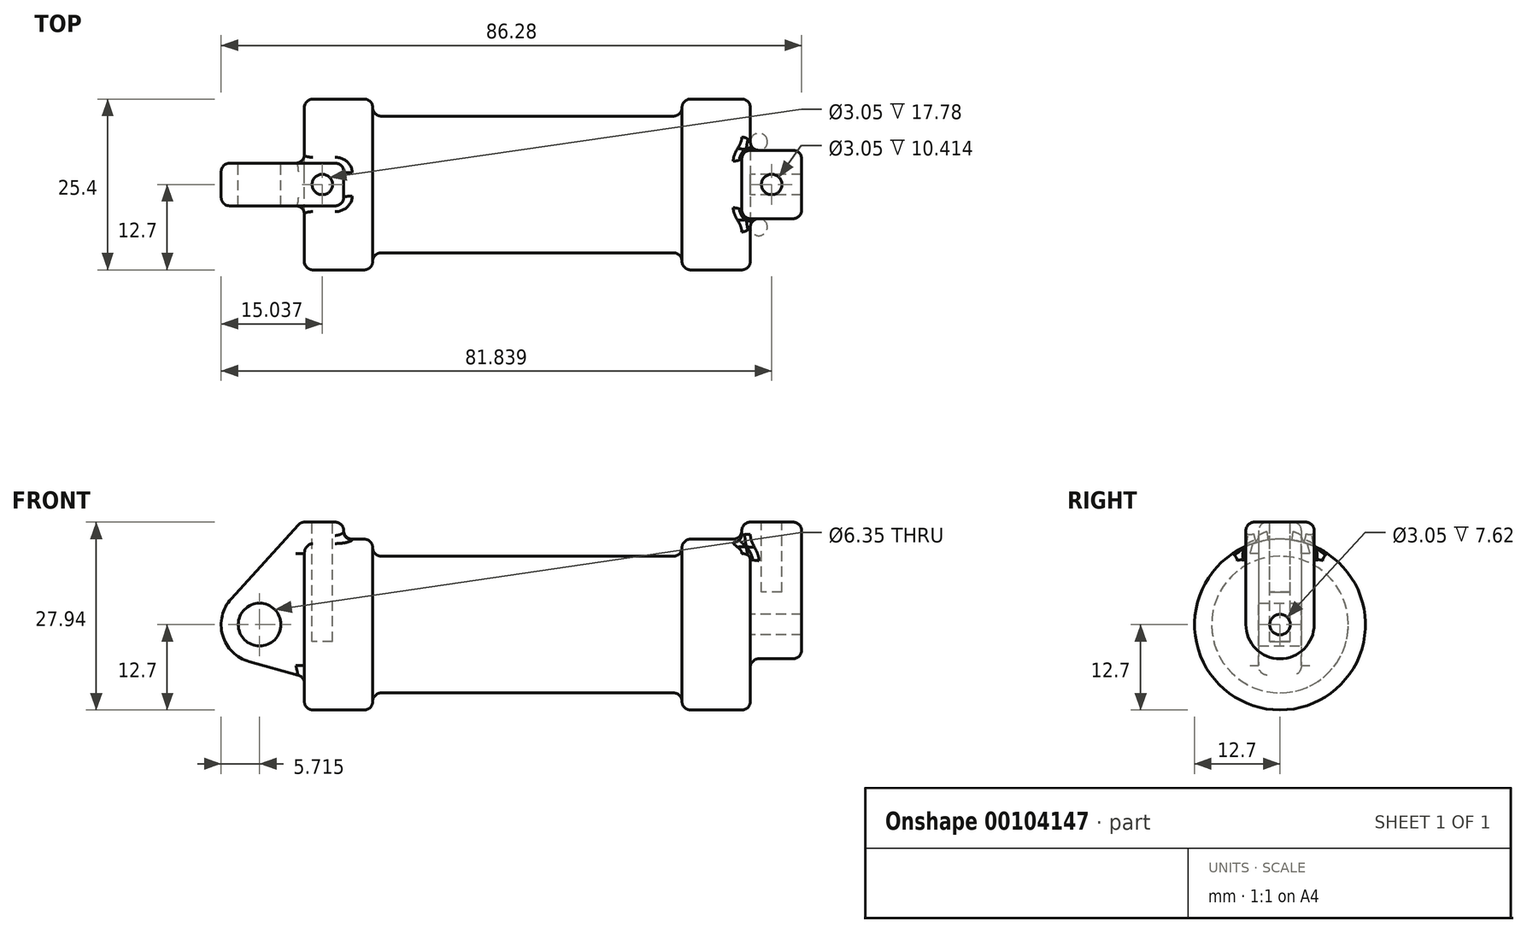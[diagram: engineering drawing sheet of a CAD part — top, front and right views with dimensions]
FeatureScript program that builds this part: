
annotation { "Feature Type Name" : "Feature", "Feature Type Description" : "" }
export const myFeature = defineFeature(function(context is Context, id is Id, definition is map)
    precondition{}
    {
        {
            var Q0;
            Q0=qCreatedBy(makeId("Front.planeOp"),FACE);
            var sketch = newSketch(context, id + "F0", { "sketchPlane" : qUnion([Q0])});
            skLineSegment(sketch, "E0", {"start": v(0, 0) * mm, "end": v(0, 12.7) * mm});
            skLineSegment(sketch, "E1", {"start": v(0, 12.7) * mm, "end": v(10.16, 12.7) * mm});
            skLineSegment(sketch, "E2", {"start": v(10.16, 12.7) * mm, "end": v(10.16, 10.16) * mm});
            skLineSegment(sketch, "E3", {"start": v(10.16, 10.16) * mm, "end": v(56.13, 10.16) * mm});
            skLineSegment(sketch, "E4", {"start": v(56.13, 10.16) * mm, "end": v(56.13, 12.7) * mm});
            skLineSegment(sketch, "E5", {"start": v(56.13, 12.7) * mm, "end": v(66.3, 12.7) * mm});
            skLineSegment(sketch, "E6", {"start": v(66.3, 12.7) * mm, "end": v(66.3, 0) * mm});
            skLineSegment(sketch, "E7", {"start": v(66.3, 0) * mm, "end": v(0, 0) * mm});
            skLineSegment(sketch, "E8", {"start": v(5.84, 15.24) * mm, "end": v(-0.5, 15.24) * mm});
            skLineSegment(sketch, "E9", {"start": v(-0.5, 15.24) * mm, "end": v(-10.88, 3.85) * mm});
            skLineSegment(sketch, "E10", {"start": v(0, 0) * mm, "end": v(-6.65, 0) * mm});
            skCircle(sketch, "E11", {"center": v(-6.65, 0) * mm, "radius": 5.72 * mm});
            skCircle(sketch, "E12", {"center": v(-6.65, 0) * mm, "radius": 3.18 * mm});
            skLineSegment(sketch, "E13", {"start": v(5.84, 15.24) * mm, "end": v(5.84, -9.4) * mm});
            skLineSegment(sketch, "E14", {"start": v(5.84, -9.4) * mm, "end": v(-8.18, -5.5) * mm});
            skSolve(sketch);
        }
        {
            var Q0;
            {var subQ0=sQuery(id+"F0.wireOp",EDGE,"E0");Q0=makeQuery(id+"F0.imprint","IMPRINT",FACE,{"disambiguationData":[TD([[makeQuery(id+"F0.imprint","IMPRINT",EDGE,{"derivedFrom":subQ0}),-1.0]])]});}
            var Q1;
            {var subQ0=sQuery(id+"F0.wireOp",EDGE,"E2");Q1=makeQuery(id+"F0.imprint","IMPRINT",FACE,{"disambiguationData":[TD([[makeQuery(id+"F0.imprint","IMPRINT",EDGE,{"derivedFrom":subQ0}),-1.0]])]});}
            var Q2;
            Q2=sQuery(id+"F0.wireOp",EDGE,"E7");
            revolve(context, id + "F1", {"entities" : qUnion([Q0, Q1]), "axis" : qUnion([Q2]), "revolveType" : RevolveType.FULL});
        }
        {
            var Q0;
            {var subQ0=sQuery(id+"F0.wireOp",EDGE,"E0");Q0=makeQuery(id+"F0.imprint","IMPRINT",FACE,{"disambiguationData":[TD([[makeQuery(id+"F0.imprint","IMPRINT",EDGE,{"derivedFrom":subQ0}),-1.0]])]});}
            var Q1;
            {var subQ3=sQuery(id+"F0.wireOp",EDGE,"E0");Q1=makeQuery(id+"F0.imprint","IMPRINT",FACE,{"disambiguationData":[TD([[makeQuery(id+"F0.imprint","IMPRINT",EDGE,{"derivedFrom":subQ3}),1.0]])]});}
            var Q2;
            {var subQ0=sQuery(id+"F0.wireOp",EDGE,"E14");Q2=makeQuery(id+"F0.imprint","IMPRINT",FACE,{"disambiguationData":[TD([[makeQuery(id+"F0.imprint","IMPRINT",EDGE,{"derivedFrom":subQ0}),-1.0]])]});}
            var Q3;
            {var subQ4=sQuery(id+"F0.wireOp",EDGE,"E12");Q3=makeQuery(id+"F0.imprint","IMPRINT",FACE,{"disambiguationData":[TD([[makeQuery(id+"F0.imprint","IMPRINT",EDGE,{"derivedFrom":subQ4}),-1.0]])]});}
            extrude(context, id + "F2", {"entities" : qUnion([Q0, Q1, Q2, Q3]), "operationType" : NewBodyOperationType.ADD, "endBound" : BoundingType.SYMMETRIC, "depth" : 6.35 * mm});
        }
        {
            var Q0;
            Q0=makeQuery(id+"F1.opRevolve","SWEPT_FACE",FACE,{"disambiguationData":[OSD([sQuery(id+"F0.wireOp",EDGE,"E6")])]});
            var sketch = newSketch(context, id + "F3", { "sketchPlane" : qUnion([Q0])});
            skCircle(sketch, "E15", {"center": v(0, 0) * mm, "radius": 1.52 * mm});
            skCircle(sketch, "E16", {"center": v(0, 0) * mm, "radius": 5.08 * mm});
            skLineSegment(sketch, "E17", {"start": v(-5.08, 0) * mm, "end": v(-5.08, 15.24) * mm});
            skLineSegment(sketch, "E18", {"start": v(5.08, 0) * mm, "end": v(5.08, 15.24) * mm});
            skLineSegment(sketch, "E19", {"start": v(-5.08, 15.24) * mm, "end": v(5.08, 15.24) * mm});
            skSolve(sketch);
        }
        {
            var Q0;
            {var subQ0=sQuery(id+"F3.wireOp",EDGE,"E17");var subQ1=sQuery(id+"F3.wireOp",EDGE,"E16");var subQ2=makeQuery(id+"F3.imprint","INTERSECT",VERTEX,{"derivedFrom":[subQ1,subQ0]});Q0=makeQuery(id+"F3.imprint","IMPRINT",FACE,{"disambiguationData":[TD([[makeQuery(id+"F3.imprint","IMPRINT",EDGE,{"disambiguationData":[TD([[subQ2,1.0]])],"derivedFrom":subQ1}),-1.0]])]});}
            var Q1;
            Q1=makeQuery(id+"F3.imprint","IMPRINT",FACE,{"disambiguationData":[TD([[makeQuery(id+"F3.imprint","IMPRINT",EDGE,{"derivedFrom":sQuery(id+"F3.wireOp",EDGE,"E15")}),-1.0]])]});
            var Q2;
            {var subQ0=sQuery(id+"F3.wireOp",EDGE,"E19");Q2=makeQuery(id+"F3.imprint","IMPRINT",FACE,{"disambiguationData":[TD([[makeQuery(id+"F3.imprint","IMPRINT",EDGE,{"derivedFrom":subQ0}),-1.0]])]});}
            extrude(context, id + "F4", {"entities" : qUnion([Q0, Q1, Q2]), "operationType" : NewBodyOperationType.ADD, "depth" : 7.62 * mm, "hasSecondDirection" : true, "secondDirectionOppositeDirection" : true, "secondDirectionDepth" : 1.27 * mm});
        }
        {
            var Q0;
            Q0=makeQuery(id+"F2.opExtrude","SWEPT_FACE",FACE,{"disambiguationData":[OSD([sQuery(id+"F0.wireOp",EDGE,"E8")])]});
            var sketch = newSketch(context, id + "F5", { "sketchPlane" : qUnion([Q0])});
            skLineSegment(sketch, "E20", {"start": v(-0.5, 0) * mm, "end": v(5.84, 0) * mm, "construction": true});
            skCircle(sketch, "E21", {"center": v(2.67, 0) * mm, "radius": 1.52 * mm});
            skSolve(sketch);
        }
        {
            var Q0;
            Q0=makeQuery(id+"F4.opExtrude","SWEPT_FACE",FACE,{"disambiguationData":[OSD([sQuery(id+"F3.wireOp",EDGE,"E19")])]});
            var sketch = newSketch(context, id + "F6", { "sketchPlane" : qUnion([Q0])});
            skLineSegment(sketch, "E22", {"start": v(65.02, 0) * mm, "end": v(73.91, 0) * mm, "construction": true});
            skCircle(sketch, "E23", {"center": v(69.47, 0) * mm, "radius": 1.52 * mm});
            skSolve(sketch);
        }
        {
            var Q0;
            Q0=makeQuery(id+"F5.imprint","IMPRINT",FACE,{"disambiguationData":[TD([[makeQuery(id+"F5.imprint","IMPRINT",EDGE,{"derivedFrom":sQuery(id+"F5.wireOp",EDGE,"E21")}),1.0]])]});
            extrude(context, id + "F7", {"entities" : qUnion([Q0]), "operationType" : NewBodyOperationType.REMOVE, "oppositeDirection" : true, "depth" : 17.78 * mm});
        }
        {
            var Q0;
            Q0=makeQuery(id+"F6.imprint","IMPRINT",FACE,{"disambiguationData":[TD([[makeQuery(id+"F6.imprint","IMPRINT",EDGE,{"derivedFrom":sQuery(id+"F6.wireOp",EDGE,"E23")}),1.0]])]});
            extrude(context, id + "F8", {"entities" : qUnion([Q0]), "operationType" : NewBodyOperationType.REMOVE, "oppositeDirection" : true, "depth" : 10.4 * mm});
        }
        {
            var Q0;
            Q0=makeQuery(id+"F1.opRevolve","SWEPT_EDGE",EDGE,{"disambiguationData":[OSD([sQuery(id+"F0.wireOp",EDGE,"E4"),sQuery(id+"F0.wireOp",EDGE,"E5")])]});
            var Q1;
            Q1=makeQuery(id+"F1.opRevolve","SWEPT_EDGE",EDGE,{"disambiguationData":[OSD([sQuery(id+"F0.wireOp",EDGE,"E5"),sQuery(id+"F0.wireOp",EDGE,"E6")])]});
            var Q2;
            Q2=makeQuery(id+"F4.opExtrude","CAP_EDGE",EDGE,{"disambiguationData":[OSD([sQuery(id+"F3.wireOp",EDGE,"E18")])],"isStart":false});
            var Q3;
            Q3=makeQuery(id+"F1.opRevolve","SWEPT_EDGE",EDGE,{"disambiguationData":[OSD([sQuery(id+"F0.wireOp",EDGE,"E3"),sQuery(id+"F0.wireOp",EDGE,"E4")])]});
            var Q4;
            Q4=makeQuery(id+"F1.opRevolve","SWEPT_EDGE",EDGE,{"disambiguationData":[OSD([sQuery(id+"F0.wireOp",EDGE,"E0"),sQuery(id+"F0.wireOp",EDGE,"E1")])]});
            var Q5;
            Q5=makeQuery(id+"F1.opRevolve","SWEPT_EDGE",EDGE,{"disambiguationData":[OSD([sQuery(id+"F0.wireOp",EDGE,"E1"),sQuery(id+"F0.wireOp",EDGE,"E2")])]});
            var Q6;
            Q6=makeQuery(id+"F2.opExtrude","CAP_EDGE",EDGE,{"disambiguationData":[OSD([sQuery(id+"F0.wireOp",EDGE,"E13")])],"isStart":true});
            var Q7;
            Q7=makeQuery(id+"F2.opExtrude","CAP_EDGE",EDGE,{"disambiguationData":[OSD([sQuery(id+"F0.wireOp",EDGE,"E8")])],"isStart":true});
            var Q8;
            Q8=makeQuery(id+"F2.opExtrude","CAP_EDGE",EDGE,{"disambiguationData":[OSD([sQuery(id+"F0.wireOp",EDGE,"E9")])],"isStart":true});
            var Q9;
            Q9=makeQuery(id+"F2.boolean.opBoolean","INTERSECT",EDGE,{"derivedFrom":[makeQuery(id+"F1.opRevolve","SWEPT_FACE",FACE,{"disambiguationData":[OSD([sQuery(id+"F0.wireOp",EDGE,"E0")])]}),makeQuery(id+"F2.opExtrude","CAP_FACE",FACE,{"disambiguationData":[OSD([sQuery(id+"F0.wireOp",EDGE,"E8"),sQuery(id+"F0.wireOp",EDGE,"E9"),sQuery(id+"F0.wireOp",EDGE,"E11"),sQuery(id+"F0.wireOp",EDGE,"E12"),sQuery(id+"F0.wireOp",EDGE,"E13"),sQuery(id+"F0.wireOp",EDGE,"E14")])],"isStart":true})]});
            var Q10;
            Q10=makeQuery(id+"F2.opExtrude","CAP_EDGE",EDGE,{"disambiguationData":[OSD([sQuery(id+"F0.wireOp",EDGE,"E14")])],"isStart":true});
            var Q11;
            Q11=makeQuery(id+"F2.boolean.opBoolean","INTERSECT",EDGE,{"derivedFrom":[makeQuery(id+"F1.opRevolve","SWEPT_FACE",FACE,{"disambiguationData":[OSD([sQuery(id+"F0.wireOp",EDGE,"E0")])]}),makeQuery(id+"F2.opExtrude","SWEPT_FACE",FACE,{"disambiguationData":[OSD([sQuery(id+"F0.wireOp",EDGE,"E14")])]})]});
            var Q12;
            Q12=makeQuery(id+"F2.opExtrude","CAP_EDGE",EDGE,{"disambiguationData":[OSD([sQuery(id+"F0.wireOp",EDGE,"E14")])],"isStart":false});
            var Q13;
            Q13=makeQuery(id+"F2.opExtrude","SWEPT_EDGE",EDGE,{"disambiguationData":[OSD([sQuery(id+"F0.wireOp",EDGE,"E11"),sQuery(id+"F0.wireOp",EDGE,"E14")])]});
            var Q14;
            Q14=makeQuery(id+"F2.opExtrude","CAP_EDGE",EDGE,{"disambiguationData":[OSD([sQuery(id+"F0.wireOp",EDGE,"E11")])],"isStart":true});
            var Q15;
            Q15=makeQuery(id+"F2.opExtrude","SWEPT_EDGE",EDGE,{"disambiguationData":[OSD([sQuery(id+"F0.wireOp",EDGE,"E9"),sQuery(id+"F0.wireOp",EDGE,"E11")])]});
            var Q16;
            Q16=makeQuery(id+"F2.opExtrude","CAP_EDGE",EDGE,{"disambiguationData":[OSD([sQuery(id+"F0.wireOp",EDGE,"E11")])],"isStart":false});
            var Q17;
            Q17=makeQuery(id+"F2.opExtrude","CAP_EDGE",EDGE,{"disambiguationData":[OSD([sQuery(id+"F0.wireOp",EDGE,"E9")])],"isStart":false});
            var Q18;
            Q18=makeQuery(id+"F2.opExtrude","SWEPT_EDGE",EDGE,{"disambiguationData":[OSD([sQuery(id+"F0.wireOp",EDGE,"E8"),sQuery(id+"F0.wireOp",EDGE,"E9")])]});
            var Q19;
            Q19=makeQuery(id+"F2.opExtrude","CAP_EDGE",EDGE,{"disambiguationData":[OSD([sQuery(id+"F0.wireOp",EDGE,"E8")])],"isStart":false});
            var Q20;
            Q20=makeQuery(id+"F2.boolean.opBoolean","INTERSECT",EDGE,{"derivedFrom":[makeQuery(id+"F1.opRevolve","SWEPT_FACE",FACE,{"disambiguationData":[OSD([sQuery(id+"F0.wireOp",EDGE,"E1")])]}),makeQuery(id+"F2.opExtrude","CAP_FACE",FACE,{"disambiguationData":[OSD([sQuery(id+"F0.wireOp",EDGE,"E8"),sQuery(id+"F0.wireOp",EDGE,"E9"),sQuery(id+"F0.wireOp",EDGE,"E11"),sQuery(id+"F0.wireOp",EDGE,"E12"),sQuery(id+"F0.wireOp",EDGE,"E13"),sQuery(id+"F0.wireOp",EDGE,"E14")])],"isStart":false})]});
            var Q21;
            Q21=makeQuery(id+"F2.boolean.opBoolean","INTERSECT",EDGE,{"derivedFrom":[makeQuery(id+"F1.opRevolve","SWEPT_FACE",FACE,{"disambiguationData":[OSD([sQuery(id+"F0.wireOp",EDGE,"E0")])]}),makeQuery(id+"F2.opExtrude","CAP_FACE",FACE,{"disambiguationData":[OSD([sQuery(id+"F0.wireOp",EDGE,"E8"),sQuery(id+"F0.wireOp",EDGE,"E9"),sQuery(id+"F0.wireOp",EDGE,"E11"),sQuery(id+"F0.wireOp",EDGE,"E12"),sQuery(id+"F0.wireOp",EDGE,"E13"),sQuery(id+"F0.wireOp",EDGE,"E14")])],"isStart":false})]});
            var Q22;
            Q22=makeQuery(id+"F2.opExtrude","CAP_EDGE",EDGE,{"disambiguationData":[OSD([sQuery(id+"F0.wireOp",EDGE,"E13")])],"isStart":false});
            var Q23;
            Q23=makeQuery(id+"F2.opExtrude","SWEPT_EDGE",EDGE,{"disambiguationData":[OSD([sQuery(id+"F0.wireOp",EDGE,"E8"),sQuery(id+"F0.wireOp",EDGE,"E13")])]});
            var Q24;
            Q24=makeQuery(id+"F2.boolean.opBoolean","INTERSECT",EDGE,{"derivedFrom":[makeQuery(id+"F1.opRevolve","SWEPT_FACE",FACE,{"disambiguationData":[OSD([sQuery(id+"F0.wireOp",EDGE,"E1")])]}),makeQuery(id+"F2.opExtrude","SWEPT_FACE",FACE,{"disambiguationData":[OSD([sQuery(id+"F0.wireOp",EDGE,"E13")])]})]});
            var Q25;
            Q25=makeQuery(id+"F1.opRevolve","SWEPT_EDGE",EDGE,{"disambiguationData":[OSD([sQuery(id+"F0.wireOp",EDGE,"E2"),sQuery(id+"F0.wireOp",EDGE,"E3")])]});
            var Q26;
            Q26=makeQuery(id+"F2.boolean.opBoolean","INTERSECT",EDGE,{"derivedFrom":[makeQuery(id+"F1.opRevolve","SWEPT_FACE",FACE,{"disambiguationData":[OSD([sQuery(id+"F0.wireOp",EDGE,"E1")])]}),makeQuery(id+"F2.opExtrude","CAP_FACE",FACE,{"disambiguationData":[OSD([sQuery(id+"F0.wireOp",EDGE,"E8"),sQuery(id+"F0.wireOp",EDGE,"E9"),sQuery(id+"F0.wireOp",EDGE,"E11"),sQuery(id+"F0.wireOp",EDGE,"E12"),sQuery(id+"F0.wireOp",EDGE,"E13"),sQuery(id+"F0.wireOp",EDGE,"E14")])],"isStart":true})]});
            var Q27;
            Q27=makeQuery(id+"F4.opExtrude","SWEPT_EDGE",EDGE,{"disambiguationData":[OSD([sQuery(id+"F3.wireOp",EDGE,"E18"),sQuery(id+"F3.wireOp",EDGE,"E19")])]});
            var Q28;
            Q28=makeQuery(id+"F4.opExtrude","CAP_EDGE",EDGE,{"disambiguationData":[OSD([sQuery(id+"F3.wireOp",EDGE,"E18")])],"isStart":true});
            var Q29;
            Q29=makeQuery(id+"F4.boolean.opBoolean","INTERSECT",EDGE,{"derivedFrom":[makeQuery(id+"F1.opRevolve","SWEPT_FACE",FACE,{"disambiguationData":[OSD([sQuery(id+"F0.wireOp",EDGE,"E5")])]}),makeQuery(id+"F4.opExtrude","SWEPT_FACE",FACE,{"disambiguationData":[OSD([sQuery(id+"F3.wireOp",EDGE,"E18")])]})]});
            var Q30;
            Q30=makeQuery(id+"F4.opExtrude","SWEPT_EDGE",EDGE,{"disambiguationData":[OSD([sQuery(id+"F3.wireOp",EDGE,"E16"),sQuery(id+"F3.wireOp",EDGE,"E18")])]});
            var Q31;
            Q31=makeQuery(id+"F4.opExtrude","CAP_EDGE",EDGE,{"disambiguationData":[OSD([sQuery(id+"F3.wireOp",EDGE,"E16")])],"isStart":false});
            var Q32;
            Q32=makeQuery(id+"F4.boolean.opBoolean","INTERSECT",EDGE,{"derivedFrom":[makeQuery(id+"F1.opRevolve","SWEPT_FACE",FACE,{"disambiguationData":[OSD([sQuery(id+"F0.wireOp",EDGE,"E6")])]}),makeQuery(id+"F4.opExtrude","SWEPT_FACE",FACE,{"disambiguationData":[OSD([sQuery(id+"F3.wireOp",EDGE,"E16")])]})]});
            var Q33;
            Q33=makeQuery(id+"F4.boolean.opBoolean","INTERSECT",EDGE,{"derivedFrom":[makeQuery(id+"F1.opRevolve","SWEPT_FACE",FACE,{"disambiguationData":[OSD([sQuery(id+"F0.wireOp",EDGE,"E6")])]}),makeQuery(id+"F4.opExtrude","SWEPT_FACE",FACE,{"disambiguationData":[OSD([sQuery(id+"F3.wireOp",EDGE,"E18")])]})]});
            var Q34;
            Q34=makeQuery(id+"F4.opExtrude","SWEPT_EDGE",EDGE,{"disambiguationData":[OSD([sQuery(id+"F3.wireOp",EDGE,"E16"),sQuery(id+"F3.wireOp",EDGE,"E17")])]});
            var Q35;
            Q35=makeQuery(id+"F4.boolean.opBoolean","INTERSECT",EDGE,{"derivedFrom":[makeQuery(id+"F1.opRevolve","SWEPT_FACE",FACE,{"disambiguationData":[OSD([sQuery(id+"F0.wireOp",EDGE,"E6")])]}),makeQuery(id+"F4.opExtrude","SWEPT_FACE",FACE,{"disambiguationData":[OSD([sQuery(id+"F3.wireOp",EDGE,"E17")])]})]});
            var Q36;
            Q36=makeQuery(id+"F4.opExtrude","CAP_EDGE",EDGE,{"disambiguationData":[OSD([sQuery(id+"F3.wireOp",EDGE,"E17")])],"isStart":true});
            var Q37;
            Q37=makeQuery(id+"F4.boolean.opBoolean","INTERSECT",EDGE,{"derivedFrom":[makeQuery(id+"F1.opRevolve","SWEPT_FACE",FACE,{"disambiguationData":[OSD([sQuery(id+"F0.wireOp",EDGE,"E5")])]}),makeQuery(id+"F4.opExtrude","SWEPT_FACE",FACE,{"disambiguationData":[OSD([sQuery(id+"F3.wireOp",EDGE,"E17")])]})]});
            var Q38;
            Q38=makeQuery(id+"F4.opExtrude","SWEPT_EDGE",EDGE,{"disambiguationData":[OSD([sQuery(id+"F3.wireOp",EDGE,"E17"),sQuery(id+"F3.wireOp",EDGE,"E19")])]});
            var Q39;
            Q39=makeQuery(id+"F4.opExtrude","CAP_EDGE",EDGE,{"disambiguationData":[OSD([sQuery(id+"F3.wireOp",EDGE,"E19")])],"isStart":true});
            var Q40;
            Q40=makeQuery(id+"F4.opExtrude","CAP_EDGE",EDGE,{"disambiguationData":[OSD([sQuery(id+"F3.wireOp",EDGE,"E19")])],"isStart":false});
            var Q41;
            Q41=makeQuery(id+"F4.opExtrude","CAP_EDGE",EDGE,{"disambiguationData":[OSD([sQuery(id+"F3.wireOp",EDGE,"E17")])],"isStart":false});
            var Q42;
            Q42=makeQuery(id+"F4.boolean.opBoolean","INTERSECT",EDGE,{"derivedFrom":[makeQuery(id+"F1.opRevolve","SWEPT_FACE",FACE,{"disambiguationData":[OSD([sQuery(id+"F0.wireOp",EDGE,"E5")])]}),makeQuery(id+"F4.opExtrude","CAP_FACE",FACE,{"disambiguationData":[OSD([sQuery(id+"F3.wireOp",EDGE,"E15"),sQuery(id+"F3.wireOp",EDGE,"E16"),sQuery(id+"F3.wireOp",EDGE,"E17"),sQuery(id+"F3.wireOp",EDGE,"E18"),sQuery(id+"F3.wireOp",EDGE,"E19")])],"isStart":true})]});
            fillet(context, id + "F9", {"entities" : qUnion([Q0, Q1, Q2, Q3, Q4, Q5, Q6, Q7, Q8, Q9, Q10, Q11, Q12, Q13, Q14, Q15, Q16, Q17, Q18, Q19, Q20, Q21, Q22, Q23, Q24, Q25, Q26, Q27, Q28, Q29, Q30, Q31, Q32, Q33, Q34, Q35, Q36, Q37, Q38, Q39, Q40, Q41, Q42]), "radius" : 1.27 * mm, "tangentPropagation" : true, "allowEdgeOverflow" : false});
        }
    });
